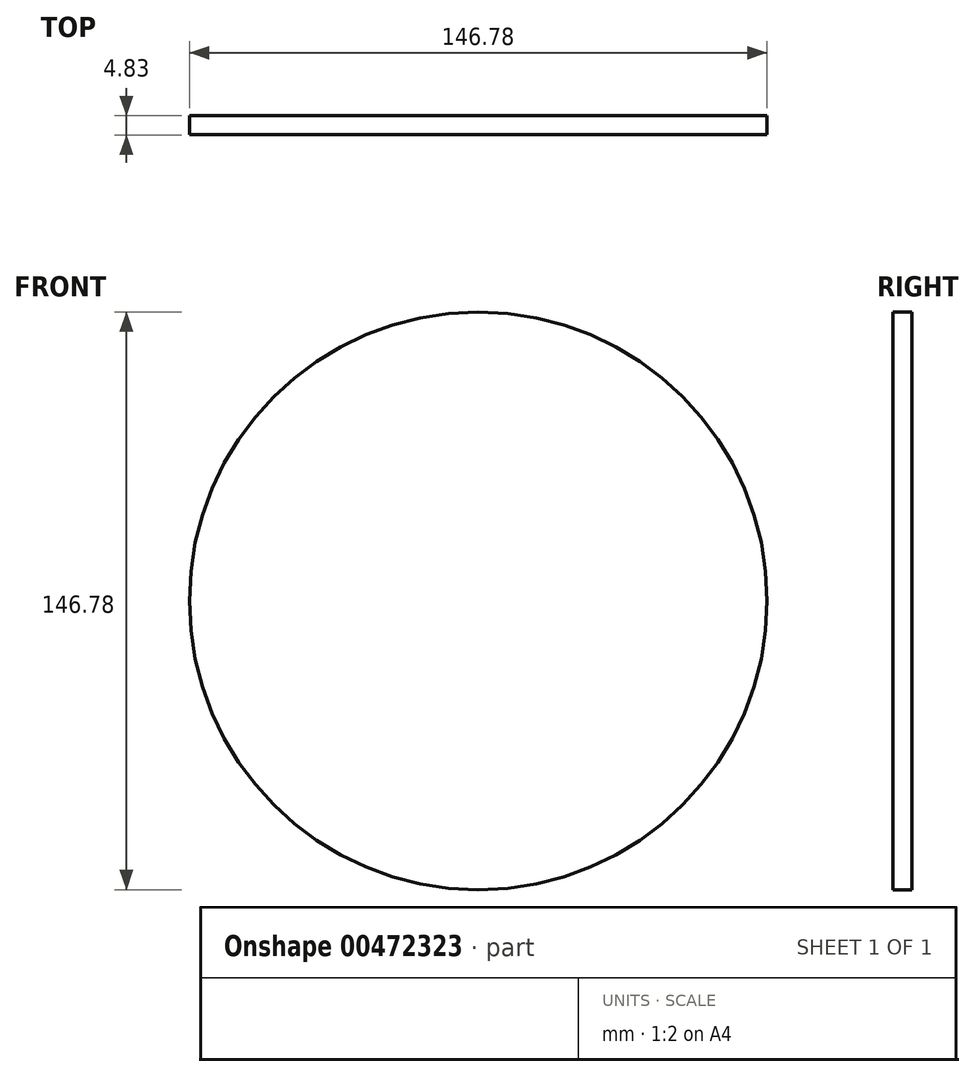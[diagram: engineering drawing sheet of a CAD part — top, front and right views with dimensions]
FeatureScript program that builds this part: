
annotation { "Feature Type Name" : "Feature", "Feature Type Description" : "" }
export const myFeature = defineFeature(function(context is Context, id is Id, definition is map)
    precondition{}
    {
        {
            var Q0;
            Q0=qCreatedBy(makeId("Front.planeOp"),FACE);
            var sketch = newSketch(context, id + "F0", { "sketchPlane" : qUnion([Q0])});
            skCircle(sketch, "E0", {"center": v(0, 0) * mm, "radius": 73.39 * mm});
            skSolve(sketch);
        }
        {
            var Q0;
            Q0 = qSketchRegion(id + "F0", true);
            extrude(context, id + "F1", {"entities" : qUnion([Q0]), "depth" : 4.83 * mm, "offsetDistance" : 25.4 * mm});
        }
    });
